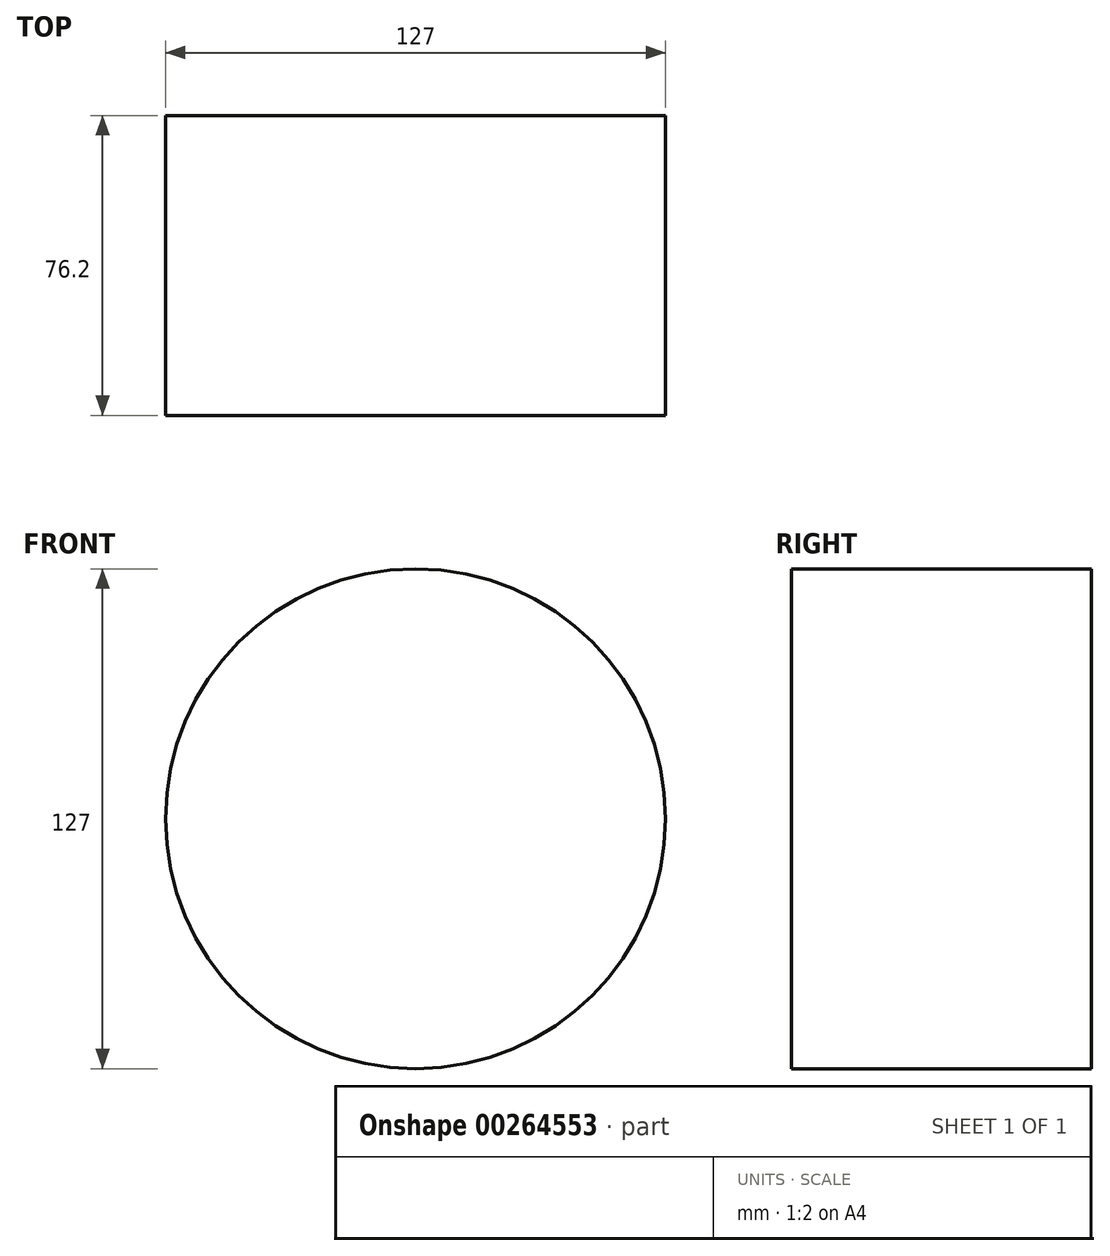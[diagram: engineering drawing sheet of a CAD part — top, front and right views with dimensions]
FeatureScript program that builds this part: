
annotation { "Feature Type Name" : "Feature", "Feature Type Description" : "" }
export const myFeature = defineFeature(function(context is Context, id is Id, definition is map)
    precondition{}
    {
        {
            var Q0;
            Q0=qCreatedBy(makeId("Front.planeOp"),FACE);
            var sketch = newSketch(context, id + "F0", { "sketchPlane" : qUnion([Q0])});
            skCircle(sketch, "E0", {"center": v(0, 0) * mm, "radius": 63.5 * mm});
            skSolve(sketch);
        }
        {
            var Q0;
            Q0=makeQuery(id+"F0.imprint","IMPRINT",FACE,{"disambiguationData":[TD([[makeQuery(id+"F0.imprint","IMPRINT",EDGE,{"derivedFrom":sQuery(id+"F0.wireOp",EDGE,"E0")}),1.0]])]});
            extrude(context, id + "F1", {"entities" : qUnion([Q0]), "depth" : 76.2 * mm});
        }
    });
